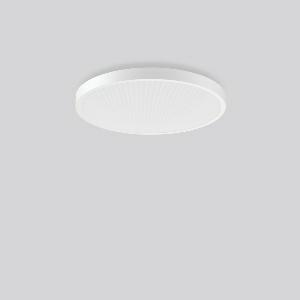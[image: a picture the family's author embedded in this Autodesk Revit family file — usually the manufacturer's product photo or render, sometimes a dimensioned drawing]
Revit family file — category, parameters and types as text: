
# Revit family: triona_round_a_312297_002_1_730_6b93
name_source: partatom
category: Lighting Fixtures
units: mm (PartAtom-declared; Revit-internal decimal feet)

## family parameters
Cut with Voids When Loaded = No
Host = Face
Light Source = No
Part Type = Normal
Room Calculation Point = No
Round Connector Dimension = Use Diameter
Shared = No

## types (1)
- TRIONA round A (1 x LED Modul 840, 6950 lm, 4000)
    Apparent Load = 64 VA
    CIE Flux Codes = 58 86 97 73 100
    Color Rendering = 80
    Color Temperature = 4000
    Default Elevation = 1800 mm
    Description = Series: TRIONA round
Decorative round LED surface-mounted luminaire. Flat, seamless frame: aluminium extrusion profile, powder coated. Cover made of sheet steel, powder-coated. Direct light emission through a diffuser plastic opal/prismatic. Indirect light emission through a flush diffuser made of satin-finish plastic. Lightguide and diffuser made of non-yellowing plastic (PMMA). Lateral light emission (RZB SIDELITE technology) for above-average homogeneous light distribution. Direct 70%, indirect 30% light emission. Suitable for Ceiling mounting, Wall (surface). Tool-free mounting via bayonet connection. Electronic ballast included. Very easy installation thanks to Plug+Play connection. With Casambi smart+free Bluetooth control for wireless network and operation using Android / iOS devices, free app available for download. Perfect for office areas (RUG < 19) and environments with computer screens in accordance with EN 12464-1. 
Colour: traffic white, matt (RAL 9016)
Diameter: 681 mm
Height: 88 mm
Lamp: LED
Socket: without socket
Colour temperature: 4000K
Colour rendering index (CRI): 80
System power: 64 W
Rated luminous flux: 6950 lm
Luminous efficiency: 109 lm/W
Control gear: Dimmable Bluetooth converter
Protection class: I
Type of protection: IP 20
    Height = 88 mm
    Lamp = 1 x LED Modul 840
    Lamp Light Flux = 6950 lm
    Lamp count = 1
    Length = 681 mm
    Lifetime = 50000 h
    Luminous efficacy = 109 lm/W
    Manufacturer = RZB
    ModVariant = No
    Model = 312297.002.1.730
    Mounting Place = Ceiling
    Mounting Type = Surface mounted
    Number of Poles = 1
    OnlyDefault = Yes
    Power Factor = 1
    Product Name = TRIONA round A
    Product group = Surface mounted modular luminaires
    ProductGroupID = 306
    Protection Class = Protection class I
    Protection Degree = IP 20
    RLX_Detail_Level = 1
    RLX_Emergency_Light_Flux = 0 lm
    RLX_Emergency_Type = 0
    RLX_Emergency_Type_DB = No
    RlxData = <blob elided: 41625 chars, md5=8dbc801d>
    Socket = socket
    Standby Power = 0 W
    System Light Flux = 6950 lm
    System Power = 64 W
    Type Comments = Product without accessories
    Type Image = 312297.002.jpg
    URL = http://relux.com
    VarID = ---
    Voltage = 230 V
    Voltage Range = 220-240 V
    Weight = 0.00 kg
    Width = 0 mm  [stored 0 ft]

note: [stored X ft] marks values corroborated as IEEE doubles in the binary element streams (Revit-internal decimal feet)

## geometry (parser evidence)
native form markers: Blend x4, Sweep x15
no freeform markers — native parametric forms only
